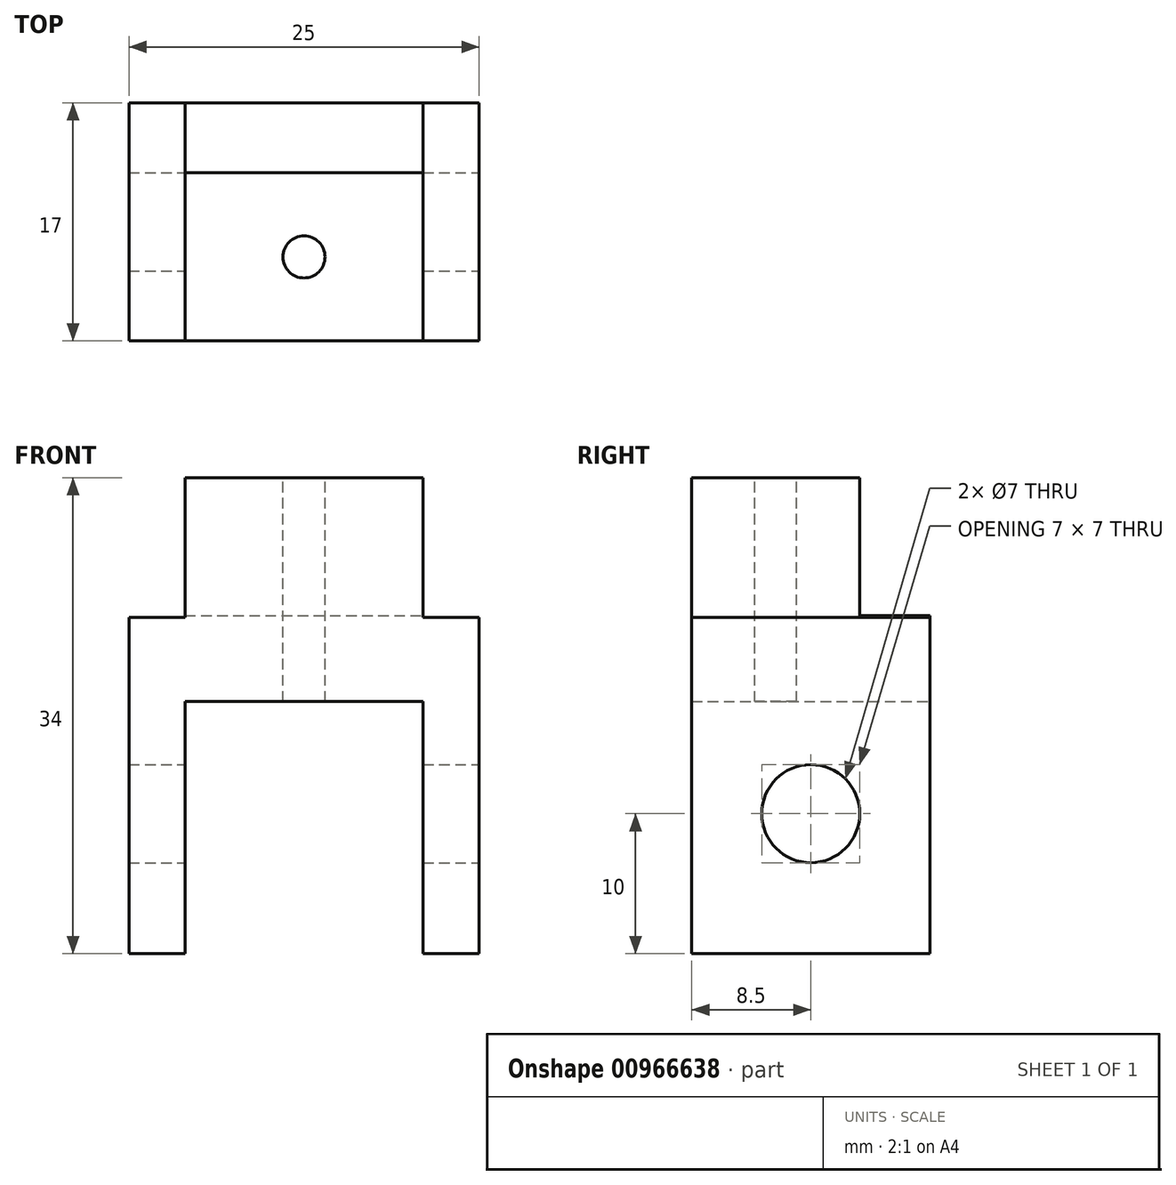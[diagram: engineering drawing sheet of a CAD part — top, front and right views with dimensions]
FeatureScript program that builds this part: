
annotation { "Feature Type Name" : "Feature", "Feature Type Description" : "" }
export const myFeature = defineFeature(function(context is Context, id is Id, definition is map)
    precondition{}
    {
        {
            var Q0;
            Q0=qCreatedBy(makeId("Front.planeOp"),FACE);
            var sketch = newSketch(context, id + "F0", { "sketchPlane" : qUnion([Q0])});
            skLineSegment(sketch, "E0.bottom", {"start": v(-8.5, 5) * mm, "end": v(8.5, 5) * mm});
            skLineSegment(sketch, "E0.top", {"start": v(-8.5, -5) * mm, "end": v(8.5, -5) * mm});
            skLineSegment(sketch, "E0.left", {"start": v(-8.5, 5) * mm, "end": v(-8.5, -5) * mm});
            skLineSegment(sketch, "E0.right", {"start": v(8.5, 5) * mm, "end": v(8.5, -5) * mm});
            skPoint(sketch, "E0.middle", {"position": v(0, 0) * mm});
            skLineSegment(sketch, "E1.bottom", {"start": v(-12.5, -5) * mm, "end": v(12.5, -5) * mm});
            skLineSegment(sketch, "E1.top", {"start": v(-12.5, -29) * mm, "end": v(-8.5, -29) * mm});
            skLineSegment(sketch, "E1.left", {"start": v(-12.5, -5) * mm, "end": v(-12.5, -29) * mm});
            skLineSegment(sketch, "E1.right", {"start": v(12.5, -5) * mm, "end": v(12.5, -29) * mm});
            skLineSegment(sketch, "E2.left", {"start": v(-12.5, -29) * mm, "end": v(-12.5, -29) * mm});
            skLineSegment(sketch, "E2.right", {"start": v(12.5, -29) * mm, "end": v(12.5, -29) * mm});
            skLineSegment(sketch, "E3.top", {"start": v(-8.5, -11) * mm, "end": v(8.5, -11) * mm});
            skLineSegment(sketch, "E3.left", {"start": v(-8.5, -29) * mm, "end": v(-8.5, -11) * mm});
            skLineSegment(sketch, "E3.right", {"start": v(8.5, -29) * mm, "end": v(8.5, -11) * mm});
            skLineSegment(sketch, "E4.trimOffspring", {"start": v(8.5, -29) * mm, "end": v(12.5, -29) * mm});
            skSolve(sketch);
        }
        {
            var Q0;
            {var subQ2=sQuery(id+"F0.wireOp",EDGE,"E0.top");var subQ6=makeQuery(id+"F0.imprint","IMPRINT",EDGE,{"derivedFrom":subQ2});Q0=qUnion([makeQuery(id+"F0.imprint","IMPRINT",FACE,{"disambiguationData":[TD([[makeQuery(id+"F0.imprint","IMPRINT",EDGE,{"derivedFrom":sQuery(id+"F0.wireOp",EDGE,"E0.bottom")}),-1.0]])]}),makeQuery(id+"F0.imprint","IMPRINT",FACE,{"disambiguationData":[TD([[subQ6,-1.0]])]})]);}
            extrude(context, id + "F1", {"entities" : qUnion([Q0]), "depth" : 17 * mm, "offsetDistance" : 25 * mm});
        }
        {
            var Q0;
            Q0=qCreatedBy(makeId("Right.planeOp"),FACE);
            var sketch = newSketch(context, id + "F2", { "sketchPlane" : qUnion([Q0])});
            skLineSegment(sketch, "E5.bottom", {"start": v(0, 5.15) * mm, "end": v(-5, 5.15) * mm});
            skLineSegment(sketch, "E5.top", {"start": v(0, -4.85) * mm, "end": v(-5, -4.85) * mm});
            skLineSegment(sketch, "E5.left", {"start": v(0, 5.15) * mm, "end": v(0, -4.85) * mm});
            skLineSegment(sketch, "E5.right", {"start": v(-5, 5.15) * mm, "end": v(-5, -4.85) * mm});
            skCircle(sketch, "E6", {"center": v(-8.5, -19) * mm, "radius": 3.5 * mm});
            skArc(sketch, "E7", {"start": v(0, -10.53) * mm, "mid": v(-7.71, -5.58) * mm, "end": v(-16.88, -5.8) * mm});
            skSolve(sketch);
        }
        {
            var Q0;
            Q0 = qSketchRegion(id + "F2", true);
            extrude(context, id + "F3", {"entities" : qUnion([Q0]), "operationType" : NewBodyOperationType.REMOVE, "endBound" : BoundingType.SYMMETRIC, "oppositeDirection" : true, "depth" : 25 * mm, "offsetDistance" : 25 * mm});
        }
        {
            var Q0;
            Q0=qCreatedBy(makeId("Top.planeOp"),FACE);
            var sketch = newSketch(context, id + "F4", { "sketchPlane" : qUnion([Q0])});
            skCircle(sketch, "E8", {"center": v(0, -11) * mm, "radius": 1.5 * mm});
            skSolve(sketch);
        }
        {
            var Q0;
            Q0 = qSketchRegion(id + "F4", true);
            extrude(context, id + "F5", {"entities" : qUnion([Q0]), "operationType" : NewBodyOperationType.REMOVE, "endBound" : BoundingType.SYMMETRIC, "oppositeDirection" : true, "depth" : 40 * mm, "offsetDistance" : 25 * mm});
        }
    });
